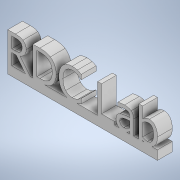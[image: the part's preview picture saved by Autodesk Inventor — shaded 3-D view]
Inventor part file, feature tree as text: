
AUTODESK INVENTOR PART (.ipt)
format: ipt  version: 2021.4 (Build 254397000, 397)  size: 291,328 bytes
history: native  units: mm
features: extrude x2, sketch x2, other x1
ambient origin geometry x8: Origin, YZ Plane, XZ Plane, XY Plane, X Axis, Y Axis, Z Axis, Center Point
bodies: Body1 (feature_tree)
feature tree (5):
  other  "ソリッド1"
  extrude  "押し出し1"  Depth=5.0mm TaperAngle=0.0deg
  extrude  "押し出し2"  Depth=3.0mm TaperAngle=0.0deg
  sketch  "スケッチ1"
  sketch  "スケッチ2"
